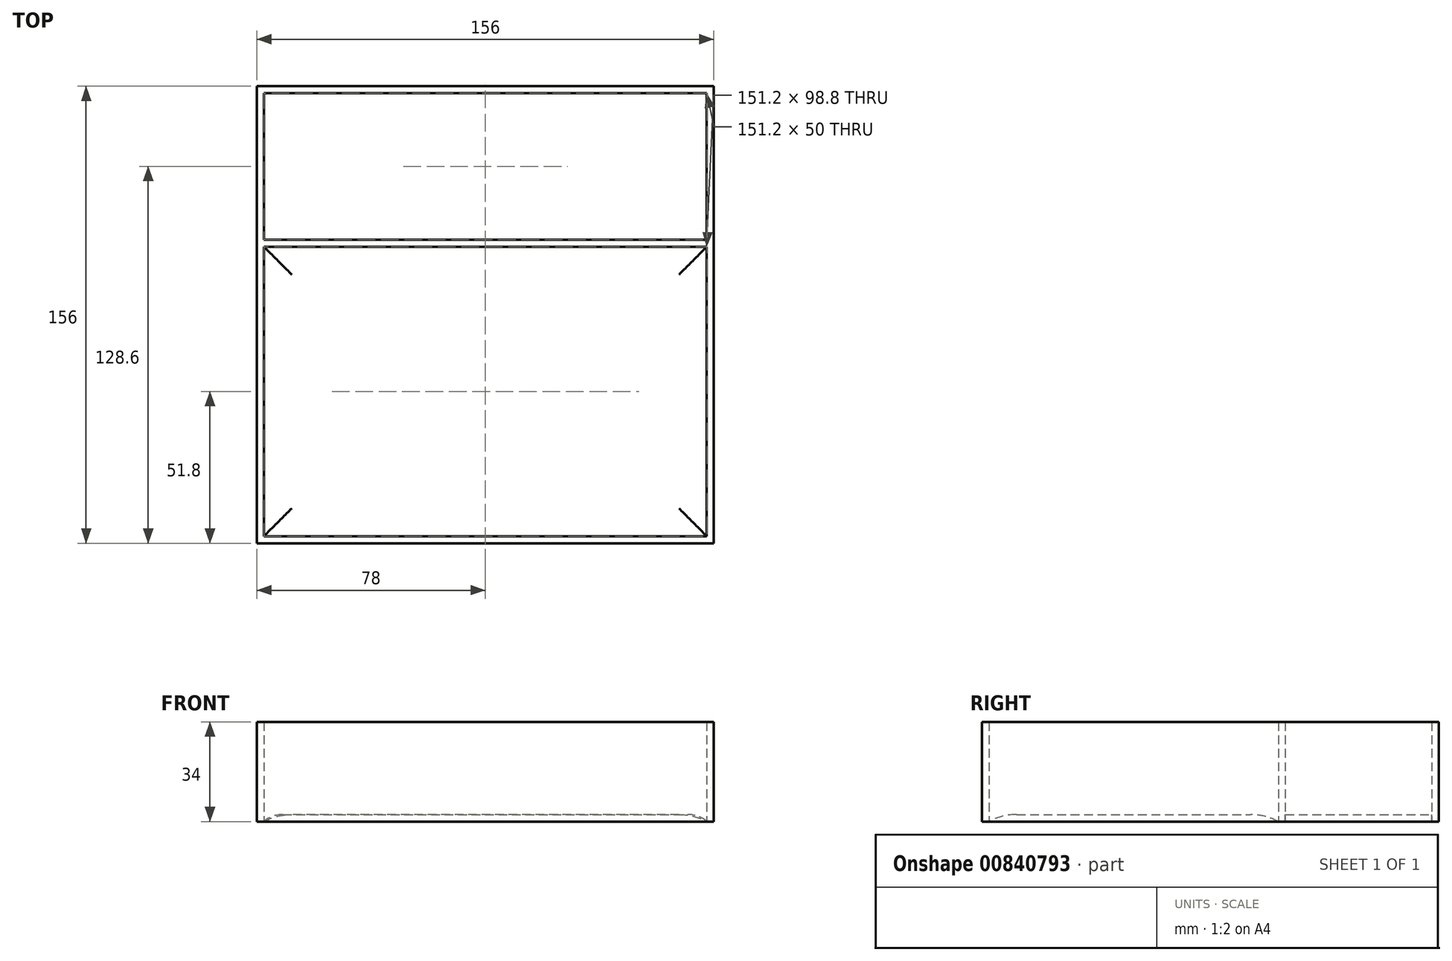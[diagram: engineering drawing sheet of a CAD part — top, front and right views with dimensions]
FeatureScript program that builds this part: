
annotation { "Feature Type Name" : "Feature", "Feature Type Description" : "" }
export const myFeature = defineFeature(function(context is Context, id is Id, definition is map)
    precondition{}
    {
        {
            var Q0;
            Q0=qCreatedBy(makeId("Top.planeOp"),FACE);
            var sketch = newSketch(context, id + "F0", { "sketchPlane" : qUnion([Q0])});
            skLineSegment(sketch, "E0.bottom", {"start": v(-78, 78) * mm, "end": v(78, 78) * mm});
            skLineSegment(sketch, "E0.top", {"start": v(-78, -78) * mm, "end": v(78, -78) * mm});
            skLineSegment(sketch, "E0.left", {"start": v(-78, 78) * mm, "end": v(-78, -78) * mm});
            skLineSegment(sketch, "E0.right", {"start": v(78, 78) * mm, "end": v(78, -78) * mm});
            skPoint(sketch, "E0.middle", {"position": v(0, 0) * mm});
            skLineSegment(sketch, "E1.0", {"start": v(-75.6, 75.6) * mm, "end": v(-75.6, -75.6) * mm});
            skLineSegment(sketch, "E1.1", {"start": v(-75.6, 75.6) * mm, "end": v(75.6, 75.6) * mm});
            skLineSegment(sketch, "E1.2", {"start": v(75.6, 75.6) * mm, "end": v(75.6, -75.6) * mm});
            skLineSegment(sketch, "E1.3", {"start": v(-75.6, -75.6) * mm, "end": v(75.6, -75.6) * mm});
            skLineSegment(sketch, "E2.0", {"start": v(-75.6, 25.6) * mm, "end": v(75.6, 25.6) * mm});
            skLineSegment(sketch, "E3.0", {"start": v(-75.6, 23.2) * mm, "end": v(75.6, 23.2) * mm});
            skSolve(sketch);
        }
        {
            var Q0;
            {var subQ0=sQuery(id+"F0.wireOp",EDGE,"E1.1");Q0=makeQuery(id+"F0.imprint","IMPRINT",FACE,{"disambiguationData":[TD([[makeQuery(id+"F0.imprint","IMPRINT",EDGE,{"derivedFrom":subQ0}),-1.0]])]});}
            var Q1;
            {var subQ0=sQuery(id+"F0.wireOp",EDGE,"E1.3");Q1=makeQuery(id+"F0.imprint","IMPRINT",FACE,{"disambiguationData":[TD([[makeQuery(id+"F0.imprint","IMPRINT",EDGE,{"derivedFrom":subQ0}),1.0]])]});}
            extrude(context, id + "F1", {"entities" : qUnion([Q0, Q1]), "depth" : 2.4 * mm, "offsetDistance" : 25 * mm});
        }
        {
            var Q0;
            {var subQ0=sQuery(id+"F0.wireOp",EDGE,"E2.0");Q0=makeQuery(id+"F0.imprint","IMPRINT",FACE,{"disambiguationData":[TD([[makeQuery(id+"F0.imprint","IMPRINT",EDGE,{"derivedFrom":subQ0}),-1.0]])]});}
            var Q1;
            Q1=makeQuery(id+"F0.imprint","IMPRINT",FACE,{"disambiguationData":[TD([[makeQuery(id+"F0.imprint","IMPRINT",EDGE,{"derivedFrom":sQuery(id+"F0.wireOp",EDGE,"E0.bottom")}),-1.0]])]});
            extrude(context, id + "F2", {"entities" : qUnion([Q0, Q1]), "depth" : 34 * mm, "offsetDistance" : 25 * mm});
        }
        {
            var Q0;
            Q0=makeQuery(id+"F1.opExtrude","CAP_EDGE",EDGE,{"disambiguationData":[OSD([sQuery(id+"F0.wireOp",EDGE,"E1.3")])],"isStart":false});
            var Q1;
            {var subQ0=sQuery(id+"F0.wireOp",EDGE,"E1.2");Q1=makeQuery(id+"F1.opExtrude","CAP_EDGE",EDGE,{"disambiguationData":[OSD([subQ0]),TDD([makeQuery(id+"F0.imprint","IMPRINT",EDGE,{"disambiguationData":[TD([[makeQuery(id+"F0.imprint","INTERSECT",VERTEX,{"derivedFrom":[subQ0,sQuery(id+"F0.wireOp",EDGE,"E1.3")]}),1.0]])],"derivedFrom":subQ0})])],"isStart":false});}
            var Q2;
            Q2=makeQuery(id+"F1.opExtrude","CAP_EDGE",EDGE,{"disambiguationData":[OSD([sQuery(id+"F0.wireOp",EDGE,"E3.0")])],"isStart":false});
            var Q3;
            {var subQ0=sQuery(id+"F0.wireOp",EDGE,"E1.0");Q3=makeQuery(id+"F1.opExtrude","CAP_EDGE",EDGE,{"disambiguationData":[OSD([subQ0]),TDD([makeQuery(id+"F0.imprint","IMPRINT",EDGE,{"disambiguationData":[TD([[makeQuery(id+"F0.imprint","INTERSECT",VERTEX,{"derivedFrom":[subQ0,sQuery(id+"F0.wireOp",EDGE,"E1.3")]}),1.0]])],"derivedFrom":subQ0})])],"isStart":false});}
            fillet(context, id + "F3", {"entities" : qUnion([Q0, Q1, Q2, Q3]), "radius" : 20 * mm, "tangentPropagation" : true, "allowEdgeOverflow" : false});
        }
        {
            var Q0;
            {var subQ0=sQuery(id+"F0.wireOp",EDGE,"E1.2");Q0=makeQuery(id+"F1.opExtrude","CAP_EDGE",EDGE,{"disambiguationData":[OSD([subQ0]),TDD([makeQuery(id+"F0.imprint","IMPRINT",EDGE,{"disambiguationData":[TD([[makeQuery(id+"F0.imprint","INTERSECT",VERTEX,{"derivedFrom":[sQuery(id+"F0.wireOp",EDGE,"E1.1"),subQ0]}),-1.0]])],"derivedFrom":subQ0})])],"isStart":false});}
            var Q1;
            {var subQ0=sQuery(id+"F0.wireOp",EDGE,"E1.0");Q1=makeQuery(id+"F1.opExtrude","CAP_EDGE",EDGE,{"disambiguationData":[OSD([subQ0]),TDD([makeQuery(id+"F0.imprint","IMPRINT",EDGE,{"disambiguationData":[TD([[makeQuery(id+"F0.imprint","INTERSECT",VERTEX,{"derivedFrom":[subQ0,sQuery(id+"F0.wireOp",EDGE,"E1.1")]}),-1.0]])],"derivedFrom":subQ0})])],"isStart":false});}
            fillet(context, id + "F4", {"entities" : qUnion([Q0, Q1]), "radius" : 10 * mm, "tangentPropagation" : true, "allowEdgeOverflow" : false});
        }
    });
